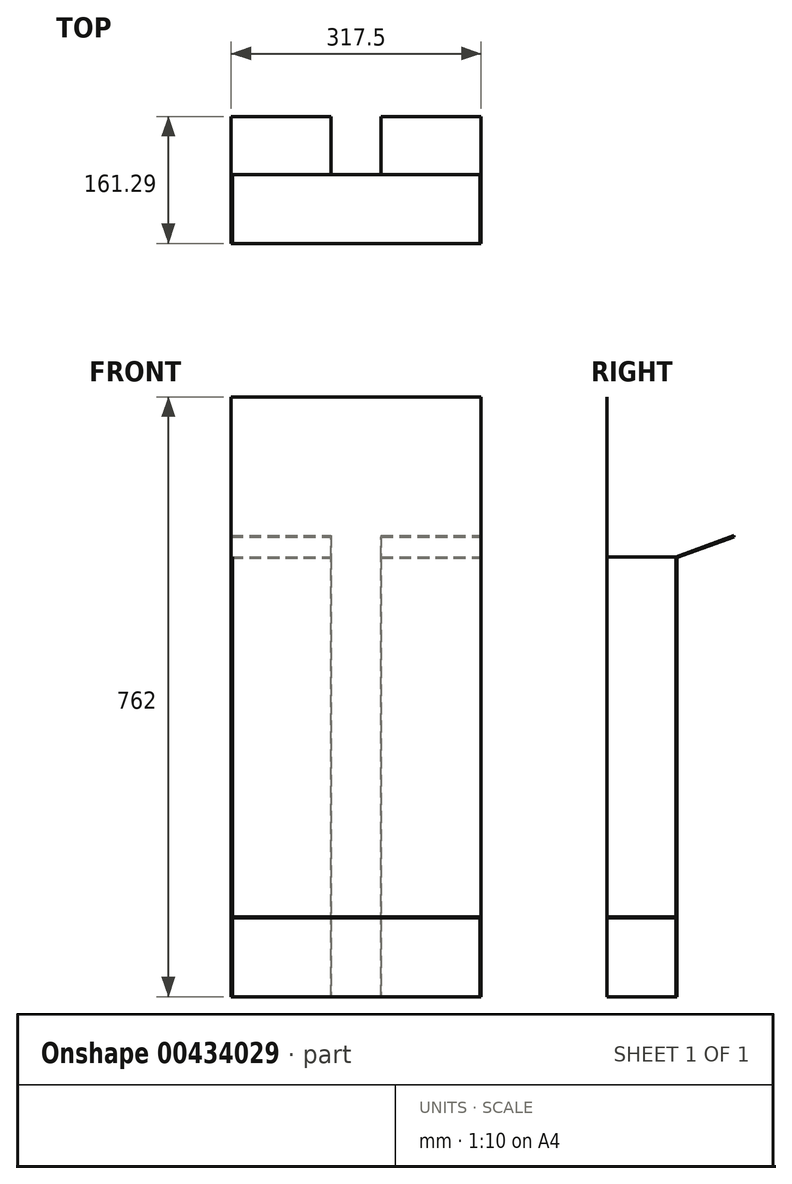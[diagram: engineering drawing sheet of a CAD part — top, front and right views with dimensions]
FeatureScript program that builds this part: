
annotation { "Feature Type Name" : "Feature", "Feature Type Description" : "" }
export const myFeature = defineFeature(function(context is Context, id is Id, definition is map)
    precondition{}
    {
        {
            var Q0;
            Q0=qCreatedBy(makeId("Front.planeOp"),FACE);
            var sketch = newSketch(context, id + "F0", { "sketchPlane" : qUnion([Q0])});
            skLineSegment(sketch, "E0.bottom", {"start": v(158.75, 381) * mm, "end": v(-158.75, 381) * mm});
            skLineSegment(sketch, "E0.top", {"start": v(158.75, -381) * mm, "end": v(-158.75, -381) * mm});
            skLineSegment(sketch, "E0.left", {"start": v(158.75, 381) * mm, "end": v(158.75, -381) * mm});
            skLineSegment(sketch, "E0.right", {"start": v(-158.75, 381) * mm, "end": v(-158.75, -381) * mm});
            skPoint(sketch, "E0.middle", {"position": v(0, 0) * mm});
            skPoint(sketch, "E1", {"position": v(158.75, 381) * mm});
            skPoint(sketch, "E2", {"position": v(-158.75, 381) * mm});
            skPoint(sketch, "E3", {"position": v(-158.75, -381) * mm});
            skPoint(sketch, "E4", {"position": v(158.75, -381) * mm});
            skSolve(sketch);
        }
        {
            var Q0;
            Q0=makeQuery(id+"F0.imprint","IMPRINT",FACE,{"disambiguationData":[TD([[makeQuery(id+"F0.imprint","IMPRINT",EDGE,{"derivedFrom":sQuery(id+"F0.wireOp",EDGE,"E0.bottom")}),1.0]])]});
            extrude(context, id + "F1", {"entities" : qUnion([Q0]), "depth" : 1 / 406.4 * mm});
        }
        {
            var Q0;
            Q0=makeQuery(id+"F1.opExtrude","SWEPT_FACE",FACE,{"disambiguationData":[OSD([sQuery(id+"F0.wireOp",EDGE,"E0.top")])]});
            var sketch = newSketch(context, id + "F2", { "sketchPlane" : qUnion([Q0])});
            skLineSegment(sketch, "E5", {"start": v(-158.75, 0) * mm, "end": v(-158.75, -88.9) * mm});
            skLineSegment(sketch, "E6", {"start": v(158.75, 0) * mm, "end": v(158.75, -88.9) * mm});
            skLineSegment(sketch, "E7", {"start": v(-158.75, -88.9) * mm, "end": v(158.75, -88.9) * mm});
            skLineSegment(sketch, "E8", {"start": v(-158.75, 0) * mm, "end": v(158.75, 0) * mm});
            skSolve(sketch);
        }
        {
            var Q0;
            Q0=makeQuery(id+"F2.imprint","IMPRINT",FACE,{"disambiguationData":[TD([[makeQuery(id+"F2.imprint","IMPRINT",EDGE,{"derivedFrom":sQuery(id+"F2.wireOp",EDGE,"E5")}),1.0]])]});
            extrude(context, id + "F3", {"entities" : qUnion([Q0]), "depth" : 1 / 406.4 * mm});
        }
        {
            var Q0;
            Q0=makeQuery(id+"F3.opExtrude","SWEPT_FACE",FACE,{"disambiguationData":[OSD([sQuery(id+"F2.wireOp",EDGE,"E7")])]});
            var sketch = newSketch(context, id + "F4", { "sketchPlane" : qUnion([Q0])});
            skLineSegment(sketch, "E9", {"start": v(-158.75, -381) * mm, "end": v(-158.75, 177.8) * mm});
            skLineSegment(sketch, "E10", {"start": v(158.75, -381) * mm, "end": v(158.75, 177.8) * mm});
            skLineSegment(sketch, "E11", {"start": v(-158.75, 177.8) * mm, "end": v(158.75, 177.8) * mm});
            skSolve(sketch);
        }
        {
            var Q0;
            Q0=makeQuery(id+"F4.imprint","IMPRINT",FACE,{"disambiguationData":[TD([[makeQuery(id+"F4.imprint","IMPRINT",EDGE,{"derivedFrom":sQuery(id+"F4.wireOp",EDGE,"E9")}),-1.0]])]});
            extrude(context, id + "F5", {"entities" : qUnion([Q0]), "operationType" : NewBodyOperationType.ADD, "oppositeDirection" : true, "depth" : 1 / 406.4 * mm});
        }
        {
            var Q0;
            Q0=makeQuery(id+"F5.boolean.opBoolean","MERGE",FACE,{"derivedFrom":[makeQuery(id+"F3.opExtrude","SWEPT_FACE",FACE,{"disambiguationData":[OSD([sQuery(id+"F2.wireOp",EDGE,"E6")])]}),makeQuery(id+"F5.opExtrude","SWEPT_FACE",FACE,{"disambiguationData":[OSD([sQuery(id+"F4.wireOp",EDGE,"E9")])]})]});
            var sketch = newSketch(context, id + "F6", { "sketchPlane" : qUnion([Q0])});
            skLineSegment(sketch, "E12", {"start": v(88.9, 177.8) * mm, "end": v(161.3, 177.8) * mm, "construction": true});
            skLineSegment(sketch, "E13", {"start": v(161.3, 177.8) * mm, "end": v(161.3, 204.79) * mm, "construction": true});
            skLineSegment(sketch, "E14", {"start": v(87.31, 177.8) * mm, "end": v(161.3, 204.79) * mm});
            skLineSegment(sketch, "E15", {"start": v(161.3, 204.79) * mm, "end": v(161.3, 203.2) * mm});
            skLineSegment(sketch, "E16", {"start": v(87.31, 177.8) * mm, "end": v(87.31, 176.21) * mm});
            skLineSegment(sketch, "E17", {"start": v(87.31, 176.21) * mm, "end": v(161.3, 203.2) * mm});
            skLineSegment(sketch, "E18", {"start": v(87.31, 177.8) * mm, "end": v(0, 177.8) * mm});
            skLineSegment(sketch, "E19", {"start": v(0, 177.8) * mm, "end": v(0, -381) * mm});
            skLineSegment(sketch, "E20", {"start": v(0, -381) * mm, "end": v(87.31, -381) * mm});
            skLineSegment(sketch, "E21", {"start": v(87.31, -381) * mm, "end": v(87.31, 177.8) * mm});
            skPoint(sketch, "E22", {"position": v(87.31, 177.8) * mm});
            skPoint(sketch, "E23", {"position": v(0, 177.8) * mm});
            skPoint(sketch, "E24", {"position": v(0, -381) * mm});
            skPoint(sketch, "E25", {"position": v(87.31, -381) * mm});
            skLineSegment(sketch, "E26", {"start": v(0, -381) * mm, "end": v(0, -279.4) * mm});
            skLineSegment(sketch, "E27", {"start": v(0, -279.4) * mm, "end": v(87.31, -279.4) * mm});
            skLineSegment(sketch, "E28", {"start": v(87.31, -279.4) * mm, "end": v(87.31, -381) * mm});
            skLineSegment(sketch, "E29.0", {"start": v(0, -280.99) * mm, "end": v(87.31, -280.99) * mm});
            skLineSegment(sketch, "E30", {"start": v(0, -279.4) * mm, "end": v(0, -280.99) * mm});
            skLineSegment(sketch, "E31", {"start": v(87.31, -279.4) * mm, "end": v(87.31, -280.99) * mm});
            skSolve(sketch);
        }
        {
            var Q0;
            Q0=makeQuery(id+"F6.imprint","IMPRINT",FACE,{"disambiguationData":[TD([[makeQuery(id+"F6.imprint","IMPRINT",EDGE,{"derivedFrom":sQuery(id+"F6.wireOp",EDGE,"E14")}),-1.0]])]});
            extrude(context, id + "F7", {"entities" : qUnion([Q0]), "operationType" : NewBodyOperationType.ADD, "oppositeDirection" : true, "depth" : 317.5 * mm});
        }
        {
            var Q0;
            {var subQ3=sQuery(id+"F6.wireOp",EDGE,"E18");Q0=makeQuery(id+"F6.imprint","IMPRINT",FACE,{"disambiguationData":[TD([[makeQuery(id+"F6.imprint","IMPRINT",EDGE,{"derivedFrom":subQ3}),1.0]])]});}
            extrude(context, id + "F8", {"entities" : qUnion([Q0]), "oppositeDirection" : true, "depth" : 1.59 * mm});
        }
        {
            var Q0;
            Q0=makeQuery(id+"F1.opExtrude","SWEPT_FACE",FACE,{"disambiguationData":[OSD([sQuery(id+"F0.wireOp",EDGE,"E0.right")])]});
            var sketch = newSketch(context, id + "F9", { "sketchPlane" : qUnion([Q0])});
            skLineSegment(sketch, "E32", {"start": v(0, -381) * mm, "end": v(-87.34, -381) * mm});
            skSolve(sketch);
        }
        {
            var Q0;
            {var subQ0=sQuery(id+"F0.wireOp",EDGE,"E0.right");Q0=makeQuery(id+"F9.imprint","IMPRINT",FACE,{"disambiguationData":[TD([[makeQuery(id+"F9.imprint","IMPRINT",EDGE,{"derivedFrom":makeQuery(id+"F1.opExtrude","CAP_EDGE",EDGE,{"disambiguationData":[OSD([subQ0])],"isStart":true})}),1.0]])]});}
            var sketch = newSketch(context, id + "F10", { "sketchPlane" : qUnion([Q0])});
            skLineSegment(sketch, "E33", {"start": v(0, 226.05) * mm, "end": v(0, -381) * mm});
            skLineSegment(sketch, "E34", {"start": v(0, -381) * mm, "end": v(-87.31, -381) * mm});
            skLineSegment(sketch, "E35", {"start": v(-87.31, -381) * mm, "end": v(-87.31, 177.86) * mm});
            skLineSegment(sketch, "E36", {"start": v(-87.31, 177.86) * mm, "end": v(0, 177.86) * mm});
            skSolve(sketch);
        }
        {
            var Q0;
            {var subQ0=sQuery(id+"F10.wireOp",EDGE,"E34");Q0=makeQuery(id+"F10.imprint","IMPRINT",FACE,{"disambiguationData":[TD([[makeQuery(id+"F10.imprint","IMPRINT",EDGE,{"derivedFrom":subQ0}),-1.0]])]});}
            extrude(context, id + "F11", {"entities" : qUnion([Q0]), "oppositeDirection" : true, "depth" : 1.59 * mm});
        }
        {
            var Q0;
            Q0=makeQuery(id+"F7.opExtrude","SWEPT_FACE",FACE,{"disambiguationData":[OSD([sQuery(id+"F6.wireOp",EDGE,"E14")])]});
            var sketch = newSketch(context, id + "F12", { "sketchPlane" : qUnion([Q0])});
            skLineSegment(sketch, "E37", {"start": v(0, 221.7) * mm, "end": v(0, 142.96) * mm});
            skLineSegment(sketch, "E38", {"start": v(0, 221.7) * mm, "end": v(-31.75, 221.7) * mm});
            skLineSegment(sketch, "E39", {"start": v(-31.75, 221.7) * mm, "end": v(-31.75, 142.96) * mm});
            skLineSegment(sketch, "E40", {"start": v(-31.75, 142.96) * mm, "end": v(0, 142.96) * mm});
            skLineSegment(sketch, "E41.MirrorCS", {"start": v(0, 221.7) * mm, "end": v(31.75, 221.7) * mm});
            skLineSegment(sketch, "E42.MirrorCS", {"start": v(31.75, 142.96) * mm, "end": v(0, 142.96) * mm});
            skLineSegment(sketch, "E43.MirrorCS", {"start": v(31.75, 221.7) * mm, "end": v(31.75, 142.96) * mm});
            skSolve(sketch);
        }
        {
            var Q0;
            Q0=makeQuery(id+"F12.imprint","IMPRINT",FACE,{"disambiguationData":[TD([[makeQuery(id+"F12.imprint","IMPRINT",EDGE,{"derivedFrom":sQuery(id+"F12.wireOp",EDGE,"E37")}),1.0]])]});
            var Q1;
            Q1=makeQuery(id+"F12.imprint","IMPRINT",FACE,{"disambiguationData":[TD([[makeQuery(id+"F12.imprint","IMPRINT",EDGE,{"derivedFrom":sQuery(id+"F12.wireOp",EDGE,"E37")}),-1.0]])]});
            extrude(context, id + "F13", {"entities" : qUnion([Q0, Q1]), "operationType" : NewBodyOperationType.REMOVE, "oppositeDirection" : true, "depth" : 1.59 * mm});
        }
        {
            var Q0;
            {var subQ0=sQuery(id+"F2.wireOp",EDGE,"E7");Q0=makeQuery(id+"F5.boolean.opBoolean","MERGE",FACE,{"derivedFrom":[makeQuery(id+"F3.opExtrude","SWEPT_FACE",FACE,{"disambiguationData":[OSD([subQ0])]}),makeQuery(id+"F5.opExtrude","CAP_FACE",FACE,{"disambiguationData":[OSD([subQ0,sQuery(id+"F4.wireOp",EDGE,"E9"),sQuery(id+"F4.wireOp",EDGE,"E10"),sQuery(id+"F4.wireOp",EDGE,"E11")])],"isStart":true})]});}
            var sketch = newSketch(context, id + "F14", { "sketchPlane" : qUnion([Q0])});
            skLineSegment(sketch, "E44", {"start": v(0, 176.69) * mm, "end": v(31.75, 176.69) * mm});
            skLineSegment(sketch, "E45", {"start": v(31.75, 176.69) * mm, "end": v(31.75, -382.59) * mm});
            skLineSegment(sketch, "E46", {"start": v(31.75, -382.59) * mm, "end": v(0, -382.59) * mm});
            skLineSegment(sketch, "E47.MirrorCS", {"start": v(0, 176.69) * mm, "end": v(-31.75, 176.69) * mm});
            skLineSegment(sketch, "E48.MirrorCS", {"start": v(-31.75, 176.69) * mm, "end": v(-31.75, -382.59) * mm});
            skLineSegment(sketch, "E49.MirrorCS", {"start": v(-31.75, -382.59) * mm, "end": v(0, -382.59) * mm});
            skSolve(sketch);
        }
        {
            var Q0;
            Q0=makeQuery(id+"F13.boolean.opBoolean","COPY",FACE,{"derivedFrom":makeQuery(id+"F13.opExtrude","SWEPT_FACE",FACE,{"disambiguationData":[OSD([sQuery(id+"F12.wireOp",EDGE,"E40"),sQuery(id+"F12.wireOp",EDGE,"E42.MirrorCS")])]})});
            extrude(context, id + "F15", {"entities" : qUnion([Q0]), "operationType" : NewBodyOperationType.REMOVE, "oppositeDirection" : true, "depth" : 2.54 * mm});
        }
        {
            var Q0;
            Q0=makeQuery(id+"F14.imprint","IMPRINT",FACE,{"disambiguationData":[TD([[makeQuery(id+"F14.imprint","IMPRINT",EDGE,{"derivedFrom":sQuery(id+"F14.wireOp",EDGE,"E44")}),-1.0]])]});
            extrude(context, id + "F16", {"entities" : qUnion([Q0]), "operationType" : NewBodyOperationType.REMOVE, "oppositeDirection" : true, "depth" : 1.59 * mm});
        }
        {
            var Q0;
            Q0=makeQuery(id+"F6.imprint","IMPRINT",FACE,{"disambiguationData":[TD([[makeQuery(id+"F6.imprint","IMPRINT",EDGE,{"derivedFrom":sQuery(id+"F6.wireOp",EDGE,"E27")}),-1.0]])]});
            extrude(context, id + "F17", {"entities" : qUnion([Q0]), "oppositeDirection" : true, "depth" : 317.5 * mm});
        }
        {
            var Q0;
            Q0=makeQuery(id+"F6.imprint","IMPRINT",FACE,{"disambiguationData":[TD([[makeQuery(id+"F6.imprint","IMPRINT",EDGE,{"derivedFrom":sQuery(id+"F6.wireOp",EDGE,"E20")}),1.0]])]});
            extrude(context, id + "F18", {"entities" : qUnion([Q0]), "oppositeDirection" : true, "depth" : 1.59 * mm});
        }
    });
